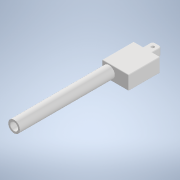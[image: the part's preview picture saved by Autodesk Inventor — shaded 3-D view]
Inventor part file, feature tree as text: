
AUTODESK INVENTOR PART (.ipt)
format: ipt  version: 2021 (Build 250183000, 183)  size: 203,264 bytes
history: native  units: mm
features: sketch x4, extrude x3, fillet x3, hole x1
ambient origin geometry x8: Origin, YZ Plane, XZ Plane, XY Plane, X Axis, Y Axis, Z Axis, Center Point
bodies: Body1 (feature_tree)
feature tree (11):
  extrude  "Extrusion2"  Depth=6.0mm
  extrude  "Extrusion3"  Depth=22.0mm
  extrude  "Extrusion4"  Depth=22.0mm
  fillet  "Fillet1"  Radius=62.0mm
  hole  "Hole1"  [1 undecoded]
  fillet  "Fillet2"  Radius=10.0mm
  fillet  "Fillet3"  Radius=35.0mm
  sketch  "Sketch1"  dims[d0=37.0mm d3=6.0mm]
  sketch  "Sketch3"  dims[d4=300.0mm d5=0.0mm d6=22.0mm]
  sketch  "Sketch5"  dims[d7=22.0mm d8=22.0mm d9=62.0mm]
  sketch  "Sketch6"  dims[d10=100.0mm d11=0.0mm d12=10.0mm d13=10.0mm d14=35.0mm d16=20.0mm d17=40.0mm d18=0.0mm d19=8.0mm d20=15.0mm d21=15.0mm d22=10.0mm d23=6.0mm d24=4.0mm d25=2.0mm d26=90.0deg d27=8.0mm d28=20.594885mm d29=2.0mm d30=2.0mm]
note: 1 required parameter value undecoded (feature->parameter linkage not recoverable at this tier; creation-order binding heuristic only, values carry confidence <= 0.55)
